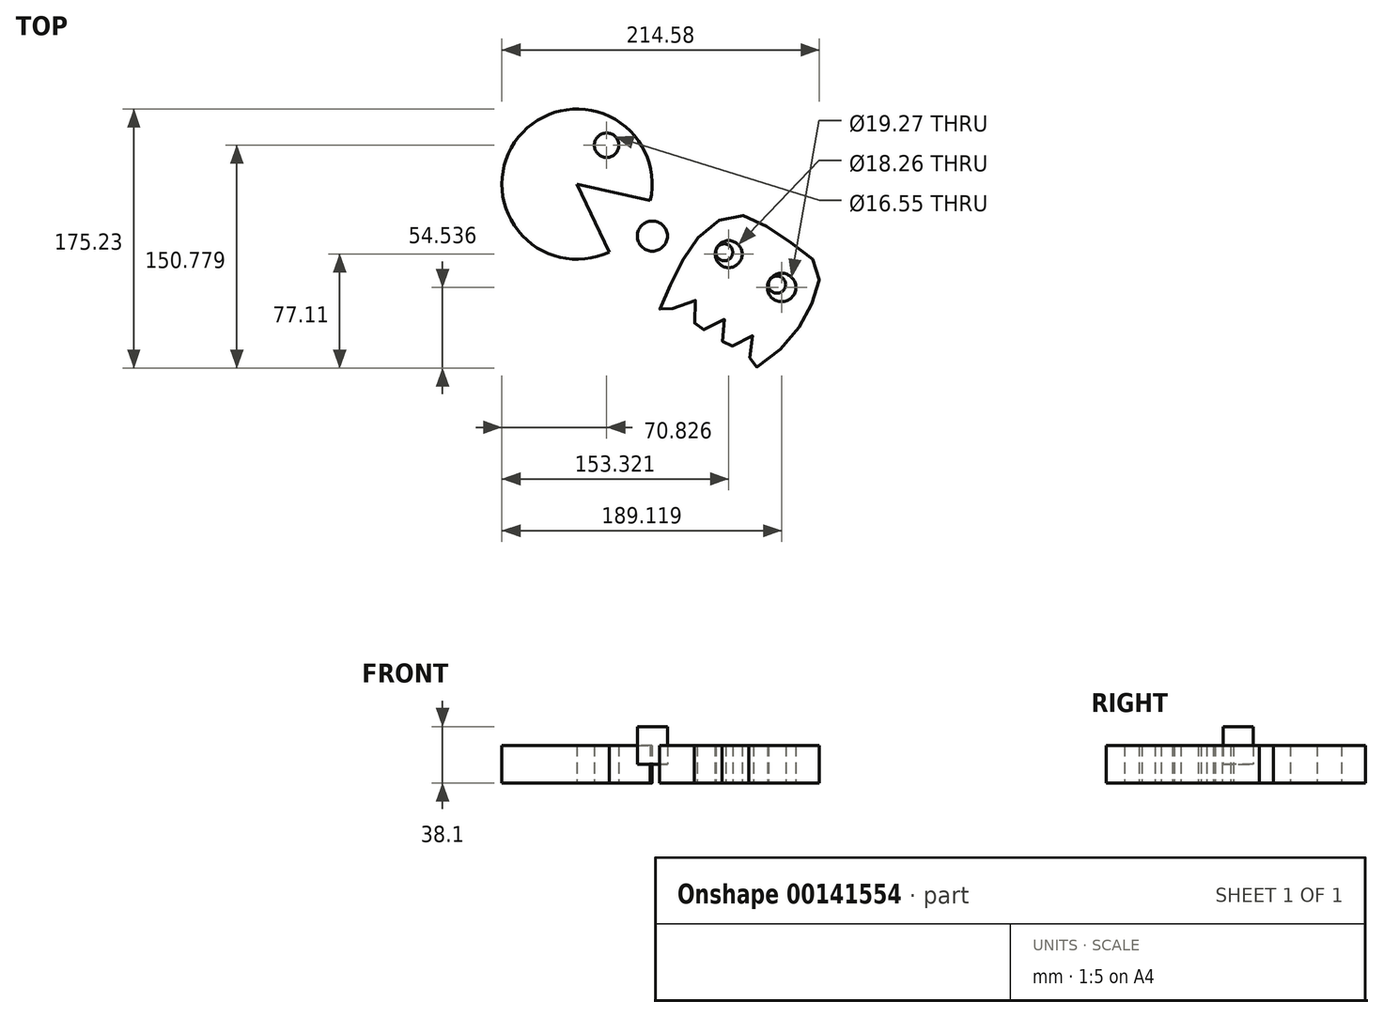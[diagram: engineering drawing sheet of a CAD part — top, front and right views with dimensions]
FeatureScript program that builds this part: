
annotation { "Feature Type Name" : "Feature", "Feature Type Description" : "" }
export const myFeature = defineFeature(function(context is Context, id is Id, definition is map)
    precondition{}
    {
        {
            var Q0;
            Q0=qCreatedBy(makeId("Top.planeOp"),FACE);
            var sketch = newSketch(context, id + "F0", { "sketchPlane" : qUnion([Q0])});
            skCircle(sketch, "E0", {"center": v(0, 0) * mm, "radius": 50.8 * mm});
            skLineSegment(sketch, "E1", {"start": v(21.78, -45.9) * mm, "end": v(0, 0) * mm});
            skLineSegment(sketch, "E2", {"start": v(0, 0) * mm, "end": v(49.55, -11.2) * mm});
            skCircle(sketch, "E3", {"center": v(20.03, 26.35) * mm, "radius": 8.28 * mm});
            skSolve(sketch);
        }
        {
            var Q0;
            {var subQ0=sQuery(id+"F0.wireOp",EDGE,"E1");Q0=makeQuery(id+"F0.imprint","IMPRINT",FACE,{"disambiguationData":[TD([[makeQuery(id+"F0.imprint","IMPRINT",EDGE,{"derivedFrom":subQ0}),1.0]])]});}
            extrude(context, id + "F1", {"entities" : qUnion([Q0]), "endBound" : BoundingType.SYMMETRIC, "depth" : 25.4 * mm});
        }
        {
            var Q0;
            Q0=qCreatedBy(makeId("Top.planeOp"),FACE);
            var sketch = newSketch(context, id + "F2", { "sketchPlane" : qUnion([Q0])});
            skCircle(sketch, "E4", {"center": v(102.52, -47.32) * mm, "radius": 9.13 * mm});
            skCircle(sketch, "E5", {"center": v(138.32, -69.9) * mm, "radius": 9.63 * mm});
            skCircle(sketch, "E6", {"center": v(99.52, -46.11) * mm, "radius": 5.74 * mm});
            skCircle(sketch, "E7", {"center": v(135.2, -67.96) * mm, "radius": 5.83 * mm});
            skFitSpline(sketch, "E8", {"points": [v(63.14, -68.1) * mm, v(57.11, -87.17) * mm, v(80.22, -78.86) * mm, v(80.17, -100.18) * mm, v(99.78, -91.54) * mm, v(98.84, -111.61) * mm, v(118.24, -102.28) * mm, v(116.52, -123.09) * mm, v(136.88, -112.33) * mm, v(158, -82.18) * mm, v(162.7, -56.57) * mm, v(137.7, -34.94) * mm, v(107.87, -20.8) * mm, v(80.68, -37.38) * mm, v(63.14, -68.1) * mm]});
            skSolve(sketch);
        }
        {
            var Q0;
            Q0=makeQuery(id+"F2.imprint","IMPRINT",FACE,{"disambiguationData":[TD([[makeQuery(id+"F2.imprint","IMPRINT",EDGE,{"derivedFrom":sQuery(id+"F2.wireOp",EDGE,"E4")}),-1.0]])]});
            var Q1;
            Q1=makeQuery(id+"F2.imprint","IMPRINT",FACE,{"disambiguationData":[TD([[makeQuery(id+"F2.imprint","IMPRINT",EDGE,{"derivedFrom":sQuery(id+"F2.wireOp",EDGE,"E6")}),1.0]])]});
            var Q2;
            Q2=makeQuery(id+"F2.imprint","IMPRINT",FACE,{"disambiguationData":[TD([[makeQuery(id+"F2.imprint","IMPRINT",EDGE,{"derivedFrom":sQuery(id+"F2.wireOp",EDGE,"E7")}),1.0]])]});
            extrude(context, id + "F3", {"entities" : qUnion([Q0, Q1, Q2]), "endBound" : BoundingType.SYMMETRIC, "depth" : 25.4 * mm});
        }
        {
            var Q0;
            Q0=qCreatedBy(makeId("Top.planeOp"),FACE);
            var sketch = newSketch(context, id + "F4", { "sketchPlane" : qUnion([Q0])});
            skCircle(sketch, "E9", {"center": v(50.95, -35.13) * mm, "radius": 10.17 * mm});
            skSolve(sketch);
        }
        {
            var Q0;
            Q0 = qSketchRegion(id + "F4", true);
            var Q1;
            Q1=makeQuery(id+"F4.imprint","IMPRINT",FACE,{"disambiguationData":[TD([[makeQuery(id+"F4.imprint","IMPRINT",EDGE,{"derivedFrom":sQuery(id+"F4.wireOp",EDGE,"E9")}),1.0]])]});
            extrude(context, id + "F5", {"entities" : qUnion([Q0, Q1]), "depth" : 25.4 * mm});
        }
    });
